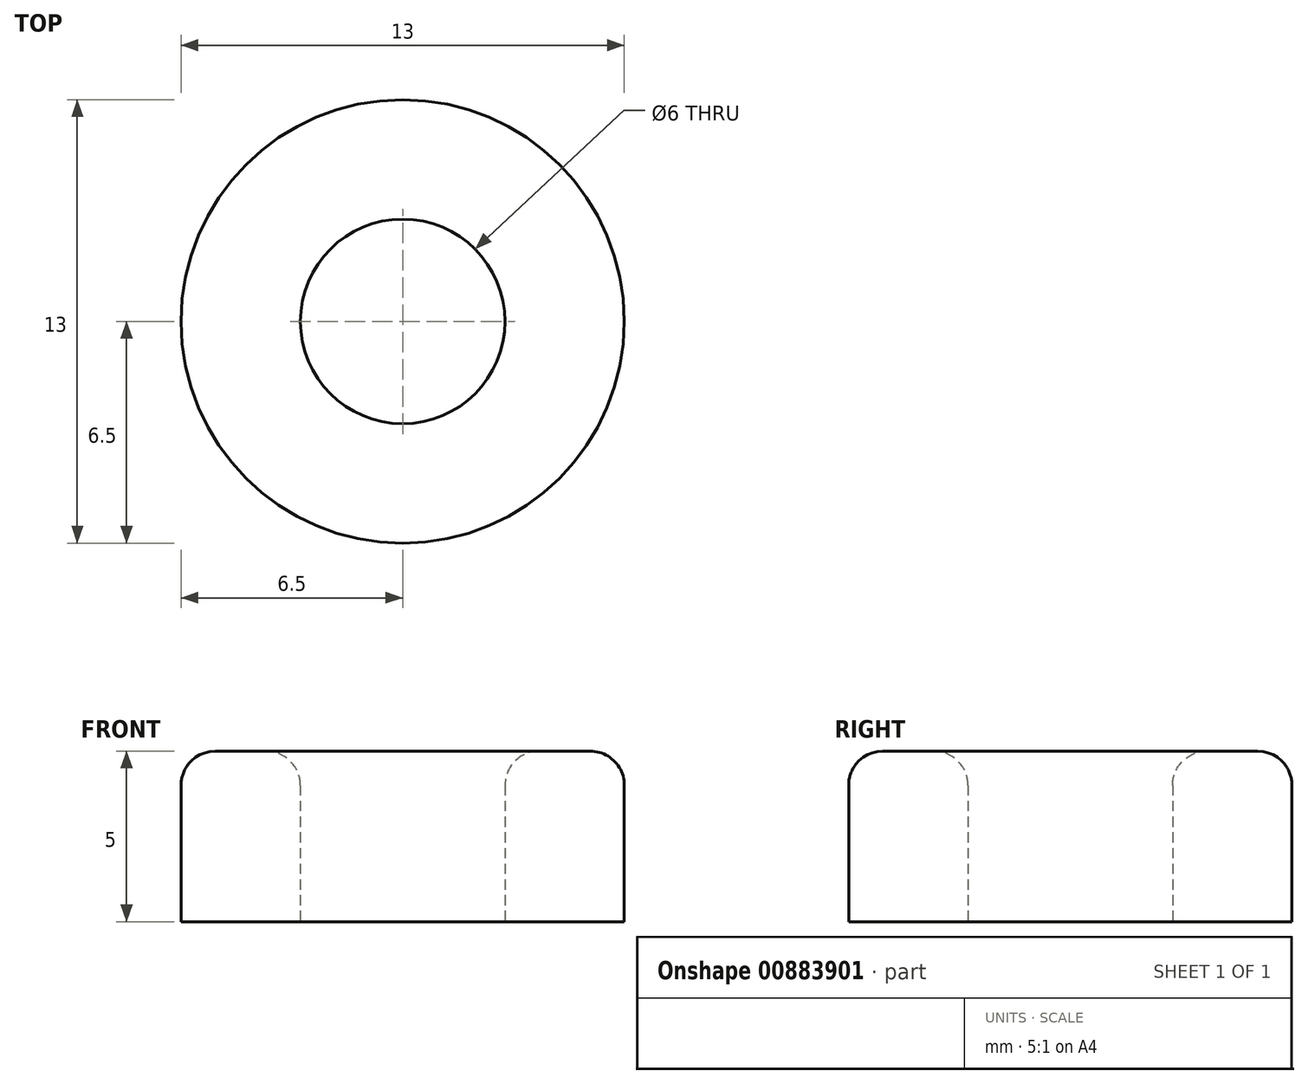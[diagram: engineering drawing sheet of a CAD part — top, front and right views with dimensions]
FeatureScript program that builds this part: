
annotation { "Feature Type Name" : "Feature", "Feature Type Description" : "" }
export const myFeature = defineFeature(function(context is Context, id is Id, definition is map)
    precondition{}
    {
        {
            var Q0;
            Q0=qCreatedBy(makeId("Top.planeOp"),FACE);
            var sketch = newSketch(context, id + "F0", { "sketchPlane" : qUnion([Q0])});
            skCircle(sketch, "E0", {"center": v(0, 0) * mm, "radius": 6.5 * mm});
            skCircle(sketch, "E1", {"center": v(0, 0) * mm, "radius": 3 * mm});
            skSolve(sketch);
        }
        {
            var Q0;
            Q0 = qSketchRegion(id + "F0", true);
            extrude(context, id + "F1", {"entities" : qUnion([Q0]), "depth" : 5 * mm, "offsetDistance" : 25 * mm});
        }
        {
            var Q0;
            Q0=makeQuery(id+"F0.imprint","IMPRINT",FACE,{"disambiguationData":[TD([[makeQuery(id+"F0.imprint","IMPRINT",EDGE,{"derivedFrom":sQuery(id+"F0.wireOp",EDGE,"E0")}),1.0]])]});
            extrude(context, id + "F2", {"entities" : qUnion([Q0]), "operationType" : NewBodyOperationType.ADD, "depth" : 5 * mm, "offsetDistance" : 25 * mm});
        }
        {
            var Q0;
            Q0=makeQuery(id+"F1.opExtrude","CAP_EDGE",EDGE,{"disambiguationData":[OSD([sQuery(id+"F0.wireOp",EDGE,"E1")])],"isStart":false});
            var Q1;
            Q1=makeQuery(id+"F1.opExtrude","CAP_EDGE",EDGE,{"disambiguationData":[OSD([sQuery(id+"F0.wireOp",EDGE,"E0")])],"isStart":false});
            fillet(context, id + "F3", {"entities" : qUnion([Q0, Q1]), "radius" : 1 * mm, "tangentPropagation" : true, "allowEdgeOverflow" : false});
        }
    });
